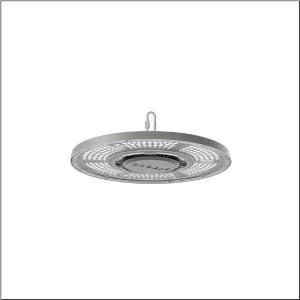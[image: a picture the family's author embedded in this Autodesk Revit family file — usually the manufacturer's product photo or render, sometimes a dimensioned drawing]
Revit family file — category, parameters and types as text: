
# Revit family: highbay_31-s_51hc42da4fmb
name_source: partatom
category: Lighting Fixtures
units: mm (PartAtom-declared; Revit-internal decimal feet)

## family parameters
Cut with Voids When Loaded = No
Host = Face
Light Source = No
Part Type = Normal
Room Calculation Point = No
Round Connector Dimension = Use Diameter
Shared = No

## types (1)
- Highbay 31-S (1 x LED, 14000 lm, 94 W, 4000K)
    Apparent Load = 94 VA
    CIE Flux Codes = 77 99 100 100 100
    Color Rendering = 80
    Color Temperature = 4000K
    Default Elevation = 1800 mm
    Description = Highbay 31-S, high bay luminaire, primary light control with lens, of PC, primary optical cover: cover panel, of PC, transparent, light emission: direct distribution, primary light characteristic: rotationally symmetric, installation type: suspended mounting, surface-mounted, LED, rated luminous flux: 14.000lm, luminous efficacy: 150lm/W, light colour: 840, colour temperature: 4000K, control gear: DALI 2, with cable, 5x 1.0mm², free wire ends, mains connection: 220..240V, AC, 50/60Hz, cable length: 1,5m, rated input power: 94W, housing, rotationally symmetric, of diecast aluminium, powder-coated, grey aluminium (RAL 9007), with hook on luminaire side, incl. screw, diameter: 339mm, protection rating (complete): IP65, insulation class (complete): insulation class I (protective earthing), certification: CE, ENEC, UKCA, protection symbol: D, impact resistance: IK08, permissible operating ambient temperature: -30..+45°C, corresponds to IFS (International Featured Standards) requirements for safety and quality in the food industry, packaging unit: 1 piece
    Height = 141 mm
    Lamp = 1 x LED
    Lamp Light Flux = 14000 lm
    Lamp Power = 94 W
    Lamp count = 1
    Length = 339 mm
    Luminous efficacy = 149 lm/W
    Manufacturer = Siteco
    ModVariant = No
    Model = 51HC42DA4FMB
    Mounting Place = Ceiling
    Mounting Type = Pendant
    Number of Poles = 1
    OnlyDefault = Yes
    Power Factor = 1
    Product Name = Highbay 31-S
    Product group = high bay luminaire
    ProductGroupID = 902
    Protection Class = Protection class I
    Protection Degree = IP 65
    RLX_Detail_Level = 1
    RLX_Emergency_Light_Flux = 0 lm
    RLX_Emergency_Type = 0
    RLX_Emergency_Type_DB = No
    RlxData = <blob elided: 162893 chars, md5=1f8122ba>
    Socket = socket
    Standby Power = 0 W
    System Light Flux = 14000 lm
    System Power = 94 W
    Type Comments = Product without accessories
    Type Image = l_1007237.jpg
    URL = http://relux.com
    VarID = ---
    Voltage = 0 V
    Weight = 0.00 kg
    Width = 0 mm  [stored 0 ft]

note: [stored X ft] marks values corroborated as IEEE doubles in the binary element streams (Revit-internal decimal feet)

## geometry (parser evidence)
native form markers: Blend x4, Sweep x9
no freeform markers — native parametric forms only
